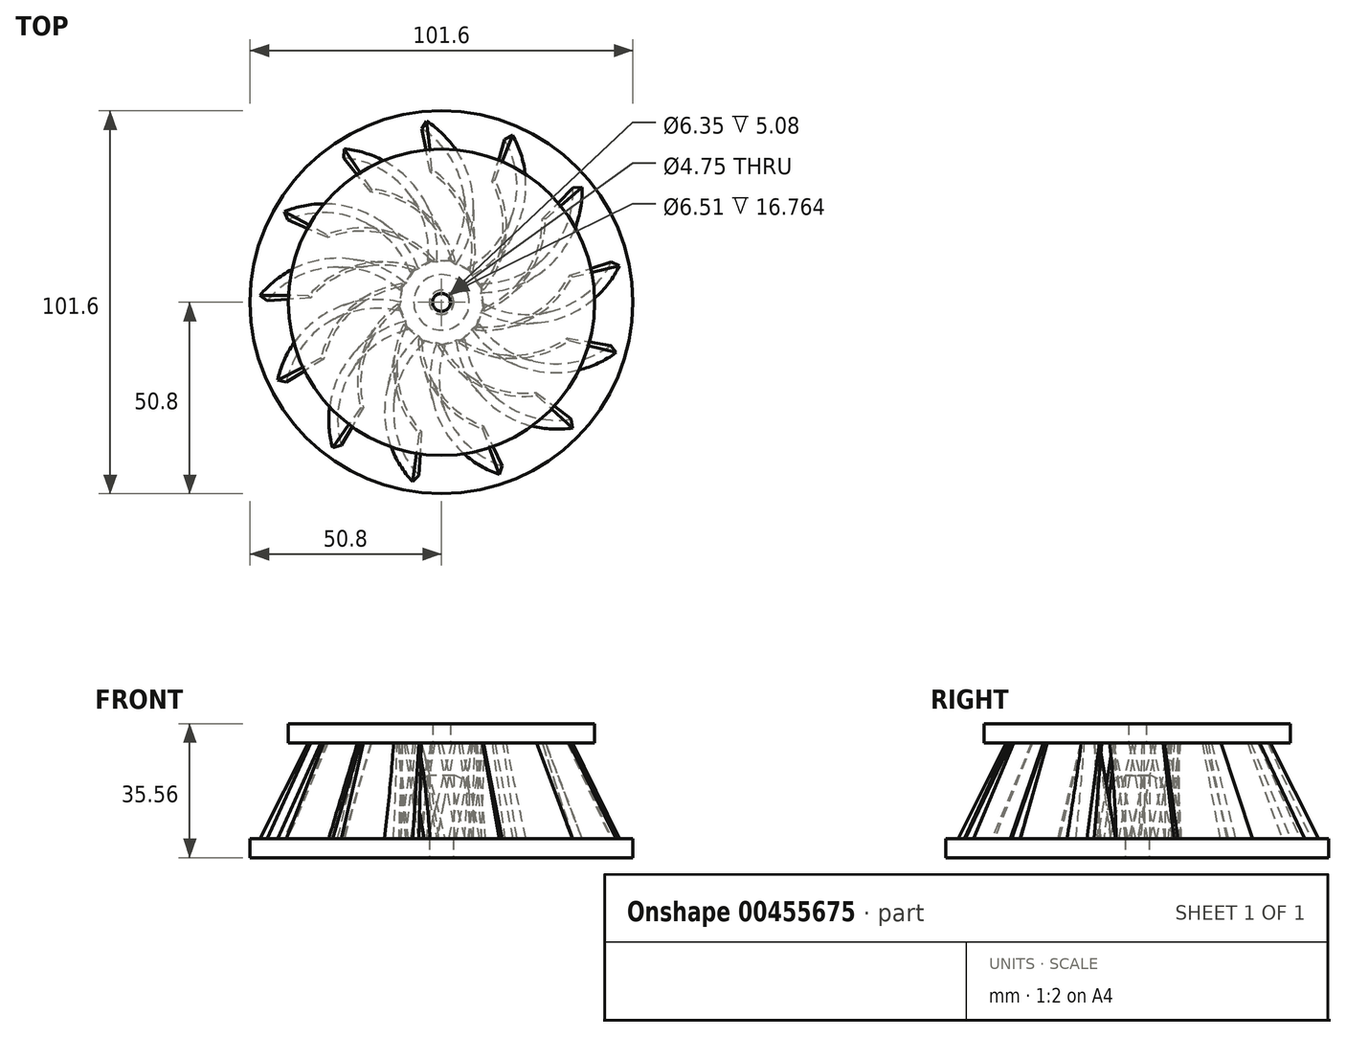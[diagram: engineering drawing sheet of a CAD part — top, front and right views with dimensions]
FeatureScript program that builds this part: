
annotation { "Feature Type Name" : "Feature", "Feature Type Description" : "" }
export const myFeature = defineFeature(function(context is Context, id is Id, definition is map)
    precondition{}
    {
        {
            var Q0;
            Q0=qCreatedBy(makeId("Top.planeOp"),FACE);
            var sketch = newSketch(context, id + "F0", { "sketchPlane" : qUnion([Q0])});
            skCircle(sketch, "E0", {"center": v(0, 0) * mm, "radius": 3.18 * mm});
            skCircle(sketch, "E1", {"center": v(0, 0) * mm, "radius": 50.8 * mm});
            skSolve(sketch);
        }
        {
            var Q0;
            Q0=makeQuery(id+"F0.imprint","IMPRINT",FACE,{"disambiguationData":[TD([[makeQuery(id+"F0.imprint","IMPRINT",EDGE,{"derivedFrom":sQuery(id+"F0.wireOp",EDGE,"E0")}),-1.0]])]});
            extrude(context, id + "F1", {"entities" : qUnion([Q0]), "depth" : 5.08 * mm, "offsetDistance" : 25.4 * mm});
        }
        {
            var Q0;
            Q0=makeQuery(id+"F1.opExtrude","CAP_FACE",FACE,{"disambiguationData":[OSD([sQuery(id+"F0.wireOp",EDGE,"E0"),sQuery(id+"F0.wireOp",EDGE,"E1")])],"isStart":false});
            var sketch = newSketch(context, id + "F2", { "sketchPlane" : qUnion([Q0])});
            skArc(sketch, "E2", {"start": v(-10.8, 0) * mm, "mid": v(-31.53, -3.45) * mm, "end": v(-43.5, -20.71) * mm});
            skArc(sketch, "E3.0", {"start": v(-11.36, -2.3) * mm, "mid": v(-30.27, -5.44) * mm, "end": v(-41.2, -21.2) * mm});
            skLineSegment(sketch, "E4", {"start": v(-43.5, -20.71) * mm, "end": v(-41.2, -21.2) * mm});
            skLineSegment(sketch, "E5", {"start": v(-11.36, -2.3) * mm, "end": v(-10.8, 0) * mm});
            skArc(sketch, "E6.1.0", {"start": v(-7.84, -8.53) * mm, "mid": v(-21.29, -22.2) * mm, "end": v(-20.87, -41.36) * mm});
            skArc(sketch, "E6.1.1", {"start": v(-8.74, -6.35) * mm, "mid": v(-23.48, -21.32) * mm, "end": v(-23.02, -42.33) * mm});
            skLineSegment(sketch, "E6.1.2", {"start": v(-23.02, -42.33) * mm, "end": v(-20.87, -41.36) * mm});
            skLineSegment(sketch, "E6.1.3", {"start": v(-7.84, -8.53) * mm, "end": v(-8.74, -6.35) * mm});
            skArc(sketch, "E6.2.0", {"start": v(-1.32, -11.51) * mm, "mid": v(-4.18, -30.47) * mm, "end": v(7.43, -45.73) * mm});
            skArc(sketch, "E6.2.1", {"start": v(-3.34, -10.28) * mm, "mid": v(-6.47, -31.05) * mm, "end": v(6.26, -47.77) * mm});
            skLineSegment(sketch, "E6.2.2", {"start": v(6.26, -47.77) * mm, "end": v(7.43, -45.73) * mm});
            skLineSegment(sketch, "E6.2.3", {"start": v(-1.32, -11.51) * mm, "end": v(-3.34, -10.28) * mm});
            skArc(sketch, "E6.3.0", {"start": v(5.7, -10.1) * mm, "mid": v(14.53, -27.1) * mm, "end": v(32.89, -32.63) * mm});
            skArc(sketch, "E6.3.1", {"start": v(3.34, -10.28) * mm, "mid": v(13.02, -28.92) * mm, "end": v(33.14, -34.97) * mm});
            skLineSegment(sketch, "E6.3.2", {"start": v(33.14, -34.97) * mm, "end": v(32.89, -32.63) * mm});
            skLineSegment(sketch, "E6.3.3", {"start": v(5.7, -10.1) * mm, "end": v(3.34, -10.28) * mm});
            skArc(sketch, "E6.4.0", {"start": v(10.54, -4.82) * mm, "mid": v(27.69, -13.39) * mm, "end": v(45.78, -7.06) * mm});
            skArc(sketch, "E6.4.1", {"start": v(8.74, -6.35) * mm, "mid": v(27.54, -15.75) * mm, "end": v(47.37, -8.81) * mm});
            skLineSegment(sketch, "E6.4.2", {"start": v(47.37, -8.81) * mm, "end": v(45.78, -7.06) * mm});
            skLineSegment(sketch, "E6.4.3", {"start": v(10.54, -4.82) * mm, "end": v(8.74, -6.35) * mm});
            skArc(sketch, "E6.5.0", {"start": v(11.36, 2.3) * mm, "mid": v(30.27, 5.44) * mm, "end": v(41.2, 21.2) * mm});
            skArc(sketch, "E6.5.1", {"start": v(10.8, 0) * mm, "mid": v(31.53, 3.45) * mm, "end": v(43.5, 20.71) * mm});
            skLineSegment(sketch, "E6.5.2", {"start": v(43.5, 20.71) * mm, "end": v(41.2, 21.2) * mm});
            skLineSegment(sketch, "E6.5.3", {"start": v(11.36, 2.3) * mm, "end": v(10.8, 0) * mm});
            skArc(sketch, "E6.6.0", {"start": v(7.84, 8.53) * mm, "mid": v(21.29, 22.2) * mm, "end": v(20.87, 41.36) * mm});
            skArc(sketch, "E6.6.1", {"start": v(8.74, 6.35) * mm, "mid": v(23.48, 21.32) * mm, "end": v(23.02, 42.33) * mm});
            skLineSegment(sketch, "E6.6.2", {"start": v(23.02, 42.33) * mm, "end": v(20.87, 41.36) * mm});
            skLineSegment(sketch, "E6.6.3", {"start": v(7.84, 8.53) * mm, "end": v(8.74, 6.35) * mm});
            skArc(sketch, "E6.7.0", {"start": v(1.32, 11.51) * mm, "mid": v(4.18, 30.47) * mm, "end": v(-7.43, 45.73) * mm});
            skArc(sketch, "E6.7.1", {"start": v(3.34, 10.28) * mm, "mid": v(6.47, 31.05) * mm, "end": v(-6.26, 47.77) * mm});
            skLineSegment(sketch, "E6.7.2", {"start": v(-6.26, 47.77) * mm, "end": v(-7.43, 45.73) * mm});
            skLineSegment(sketch, "E6.7.3", {"start": v(1.32, 11.51) * mm, "end": v(3.34, 10.28) * mm});
            skArc(sketch, "E6.8.0", {"start": v(-5.7, 10.1) * mm, "mid": v(-14.53, 27.1) * mm, "end": v(-32.89, 32.63) * mm});
            skArc(sketch, "E6.8.1", {"start": v(-3.34, 10.28) * mm, "mid": v(-13.02, 28.92) * mm, "end": v(-33.14, 34.97) * mm});
            skLineSegment(sketch, "E6.8.2", {"start": v(-33.14, 34.97) * mm, "end": v(-32.89, 32.63) * mm});
            skLineSegment(sketch, "E6.8.3", {"start": v(-5.7, 10.1) * mm, "end": v(-3.34, 10.28) * mm});
            skArc(sketch, "E6.9.0", {"start": v(-10.54, 4.82) * mm, "mid": v(-27.69, 13.39) * mm, "end": v(-45.78, 7.06) * mm});
            skArc(sketch, "E6.9.1", {"start": v(-8.74, 6.35) * mm, "mid": v(-27.54, 15.75) * mm, "end": v(-47.37, 8.81) * mm});
            skLineSegment(sketch, "E6.9.2", {"start": v(-47.37, 8.81) * mm, "end": v(-45.78, 7.06) * mm});
            skLineSegment(sketch, "E6.9.3", {"start": v(-10.54, 4.82) * mm, "end": v(-8.74, 6.35) * mm});
            skPoint(sketch, "E6.center", {"position": v(0, 0) * mm});
            skSolve(sketch);
        }
        {
            var Q0;
            Q0=makeQuery(id+"F2.imprint","IMPRINT",FACE,{"disambiguationData":[TD([[makeQuery(id+"F2.imprint","IMPRINT",EDGE,{"derivedFrom":sQuery(id+"F2.wireOp",EDGE,"E2")}),-1.0]])]});
            cPlane(context, id + "F3", {"entities" : qUnion([Q0]), "cplaneType" : CPlaneType.OFFSET, "offset" : 25.4 * mm, "width" : 152.4 * mm, "height" : 152.4 * mm});
        }
        {
            var Q0;
            Q0=qCreatedBy(id+"F3.planeOp",FACE);
            var sketch = newSketch(context, id + "F4", { "sketchPlane" : qUnion([Q0])});
            skArc(sketch, "E7.0", {"start": v(-6.2, 9.53) * mm, "mid": v(-20.67, 12.1) * mm, "end": v(-34.13, 6.2) * mm});
            skLineSegment(sketch, "E7.1", {"start": v(-6.2, 9.53) * mm, "end": v(-5.5, 10.12) * mm});
            skArc(sketch, "E7.2", {"start": v(-5.5, 10.12) * mm, "mid": v(-20.6, 12.94) * mm, "end": v(-34.7, 6.82) * mm});
            skLineSegment(sketch, "E7.3", {"start": v(-34.7, 6.82) * mm, "end": v(-34.13, 6.2) * mm});
            skArc(sketch, "E8.1.0", {"start": v(-10.61, 4.07) * mm, "mid": v(-23.83, -2.37) * mm, "end": v(-31.26, -15.05) * mm});
            skArc(sketch, "E8.1.1", {"start": v(-10.4, 4.95) * mm, "mid": v(-24.28, -1.64) * mm, "end": v(-32.08, -14.87) * mm});
            skLineSegment(sketch, "E8.1.2", {"start": v(-10.61, 4.07) * mm, "end": v(-10.4, 4.95) * mm});
            skLineSegment(sketch, "E8.1.3", {"start": v(-32.08, -14.87) * mm, "end": v(-31.26, -15.05) * mm});
            skArc(sketch, "E8.2.0", {"start": v(-10.98, -2.95) * mm, "mid": v(-17.89, -15.92) * mm, "end": v(-16.44, -30.55) * mm});
            skArc(sketch, "E8.2.1", {"start": v(-11.33, -2.1) * mm, "mid": v(-18.68, -15.6) * mm, "end": v(-17.2, -30.89) * mm});
            skLineSegment(sketch, "E8.2.2", {"start": v(-10.98, -2.95) * mm, "end": v(-11.33, -2.1) * mm});
            skLineSegment(sketch, "E8.2.3", {"start": v(-17.2, -30.89) * mm, "end": v(-16.44, -30.55) * mm});
            skArc(sketch, "E8.3.0", {"start": v(-7.15, -8.84) * mm, "mid": v(-5.11, -23.4) * mm, "end": v(4.65, -34.38) * mm});
            skArc(sketch, "E8.3.1", {"start": v(-7.92, -8.36) * mm, "mid": v(-5.94, -23.6) * mm, "end": v(4.23, -35.1) * mm});
            skLineSegment(sketch, "E8.3.2", {"start": v(-7.15, -8.84) * mm, "end": v(-7.92, -8.36) * mm});
            skLineSegment(sketch, "E8.3.3", {"start": v(4.23, -35.1) * mm, "end": v(4.65, -34.38) * mm});
            skArc(sketch, "E8.4.0", {"start": v(-0.6, -11.35) * mm, "mid": v(9.61, -21.93) * mm, "end": v(23.97, -25.08) * mm});
            skArc(sketch, "E8.4.1", {"start": v(-1.5, -11.42) * mm, "mid": v(9.06, -22.58) * mm, "end": v(24.06, -25.91) * mm});
            skLineSegment(sketch, "E8.4.2", {"start": v(-0.6, -11.35) * mm, "end": v(-1.5, -11.42) * mm});
            skLineSegment(sketch, "E8.4.3", {"start": v(24.06, -25.91) * mm, "end": v(23.97, -25.08) * mm});
            skArc(sketch, "E8.5.0", {"start": v(6.2, -9.53) * mm, "mid": v(20.67, -12.1) * mm, "end": v(34.13, -6.2) * mm});
            skArc(sketch, "E8.5.1", {"start": v(5.5, -10.12) * mm, "mid": v(20.6, -12.94) * mm, "end": v(34.7, -6.82) * mm});
            skLineSegment(sketch, "E8.5.2", {"start": v(6.2, -9.53) * mm, "end": v(5.5, -10.12) * mm});
            skLineSegment(sketch, "E8.5.3", {"start": v(34.7, -6.82) * mm, "end": v(34.13, -6.2) * mm});
            skArc(sketch, "E8.6.0", {"start": v(10.61, -4.07) * mm, "mid": v(23.83, 2.37) * mm, "end": v(31.26, 15.05) * mm});
            skArc(sketch, "E8.6.1", {"start": v(10.4, -4.95) * mm, "mid": v(24.28, 1.64) * mm, "end": v(32.08, 14.87) * mm});
            skLineSegment(sketch, "E8.6.2", {"start": v(10.61, -4.07) * mm, "end": v(10.4, -4.95) * mm});
            skLineSegment(sketch, "E8.6.3", {"start": v(32.08, 14.87) * mm, "end": v(31.26, 15.05) * mm});
            skArc(sketch, "E8.7.0", {"start": v(10.98, 2.95) * mm, "mid": v(17.89, 15.92) * mm, "end": v(16.44, 30.55) * mm});
            skArc(sketch, "E8.7.1", {"start": v(11.33, 2.1) * mm, "mid": v(18.68, 15.6) * mm, "end": v(17.2, 30.89) * mm});
            skLineSegment(sketch, "E8.7.2", {"start": v(10.98, 2.95) * mm, "end": v(11.33, 2.1) * mm});
            skLineSegment(sketch, "E8.7.3", {"start": v(17.2, 30.89) * mm, "end": v(16.44, 30.55) * mm});
            skArc(sketch, "E8.8.0", {"start": v(7.15, 8.84) * mm, "mid": v(5.11, 23.4) * mm, "end": v(-4.65, 34.38) * mm});
            skArc(sketch, "E8.8.1", {"start": v(7.92, 8.36) * mm, "mid": v(5.94, 23.6) * mm, "end": v(-4.23, 35.1) * mm});
            skLineSegment(sketch, "E8.8.2", {"start": v(7.15, 8.84) * mm, "end": v(7.92, 8.36) * mm});
            skLineSegment(sketch, "E8.8.3", {"start": v(-4.23, 35.1) * mm, "end": v(-4.65, 34.38) * mm});
            skArc(sketch, "E8.9.0", {"start": v(0.6, 11.35) * mm, "mid": v(-9.61, 21.93) * mm, "end": v(-23.97, 25.08) * mm});
            skArc(sketch, "E8.9.1", {"start": v(1.5, 11.42) * mm, "mid": v(-9.06, 22.58) * mm, "end": v(-24.06, 25.91) * mm});
            skLineSegment(sketch, "E8.9.2", {"start": v(0.6, 11.35) * mm, "end": v(1.5, 11.42) * mm});
            skLineSegment(sketch, "E8.9.3", {"start": v(-24.06, 25.91) * mm, "end": v(-23.97, 25.08) * mm});
            skPoint(sketch, "E8.center", {"position": v(0, 0) * mm});
            skSolve(sketch);
        }
        {
            var Q1;
            Q1=makeQuery(id+"F4.imprint","IMPRINT",FACE,{"disambiguationData":[TD([[makeQuery(id+"F4.imprint","IMPRINT",EDGE,{"derivedFrom":sQuery(id+"F4.wireOp",EDGE,"E8.1.0")}),-1.0]])]});
            var Q2;
            Q2=makeQuery(id+"F2.imprint","IMPRINT",FACE,{"disambiguationData":[TD([[makeQuery(id+"F2.imprint","IMPRINT",EDGE,{"derivedFrom":sQuery(id+"F2.wireOp",EDGE,"E2")}),1.0]])]});
            loft(context, id + "F5", {"operationType" : NewBodyOperationType.ADD, "sheetProfilesArray" : [{ "sheetProfileEntities" : qUnion([Q1]) }, { "sheetProfileEntities" : qUnion([Q2]) }]});
        }
        {
            var Q0;
            Q0=makeQuery(id+"F1.opExtrude","SWEPT_BODY",BODY,{"disambiguationData":[OSD([sQuery(id+"F0.wireOp",EDGE,"E0"),sQuery(id+"F0.wireOp",EDGE,"E1")])]});
            var Q1;
            Q1=makeQuery(id+"F1.opExtrude","CAP_EDGE",EDGE,{"disambiguationData":[OSD([sQuery(id+"F0.wireOp",EDGE,"E1")])],"isStart":false});
            circularPattern(context, id + "F6", {"entities" : qUnion([Q0]), "axis" : qUnion([Q1]), "angle" : 360 * degree, "instanceCount" : 13, "equalSpace" : true});
        }
        {
            var Q0;
            Q0=qCreatedBy(id+"F3.planeOp",FACE);
            var sketch = newSketch(context, id + "F7", { "sketchPlane" : qUnion([Q0])});
            skCircle(sketch, "E9", {"center": v(0, 0) * mm, "radius": 2.37 * mm});
            skCircle(sketch, "E10", {"center": v(0, 0) * mm, "radius": 40.64 * mm});
            skSolve(sketch);
        }
        {
            var Q0;
            Q0=makeQuery(id+"F1.opExtrude","CAP_FACE",FACE,{"disambiguationData":[OSD([sQuery(id+"F0.wireOp",EDGE,"E0"),sQuery(id+"F0.wireOp",EDGE,"E1")])],"isStart":false});
            var sketch = newSketch(context, id + "F8", { "sketchPlane" : qUnion([Q0])});
            skCircle(sketch, "E11", {"center": v(0, 0) * mm, "radius": 3.25 * mm});
            skCircle(sketch, "E12", {"center": v(0, 0) * mm, "radius": 7.37 * mm});
            skSolve(sketch);
        }
        {
            var Q0;
            Q0 = qSketchRegion(id + "F7", true);
            extrude(context, id + "F9", {"entities" : qUnion([Q0]), "operationType" : NewBodyOperationType.ADD, "depth" : 5.08 * mm, "offsetDistance" : 25.4 * mm});
        }
        {
            var Q0;
            Q0 = qSketchRegion(id + "F8", true);
            extrude(context, id + "F10", {"entities" : qUnion([Q0]), "operationType" : NewBodyOperationType.ADD, "depth" : 16.76 * mm, "offsetDistance" : 25.4 * mm});
        }
        {
            var Q0;
            Q0=makeQuery(id+"F10.opExtrude","CAP_EDGE",EDGE,{"disambiguationData":[OSD([sQuery(id+"F8.wireOp",EDGE,"E12")])],"isStart":false});
            fillet(context, id + "F11", {"entities" : qUnion([Q0]), "radius" : 5.08 * mm, "tangentPropagation" : true, "allowEdgeOverflow" : false});
        }
    });
